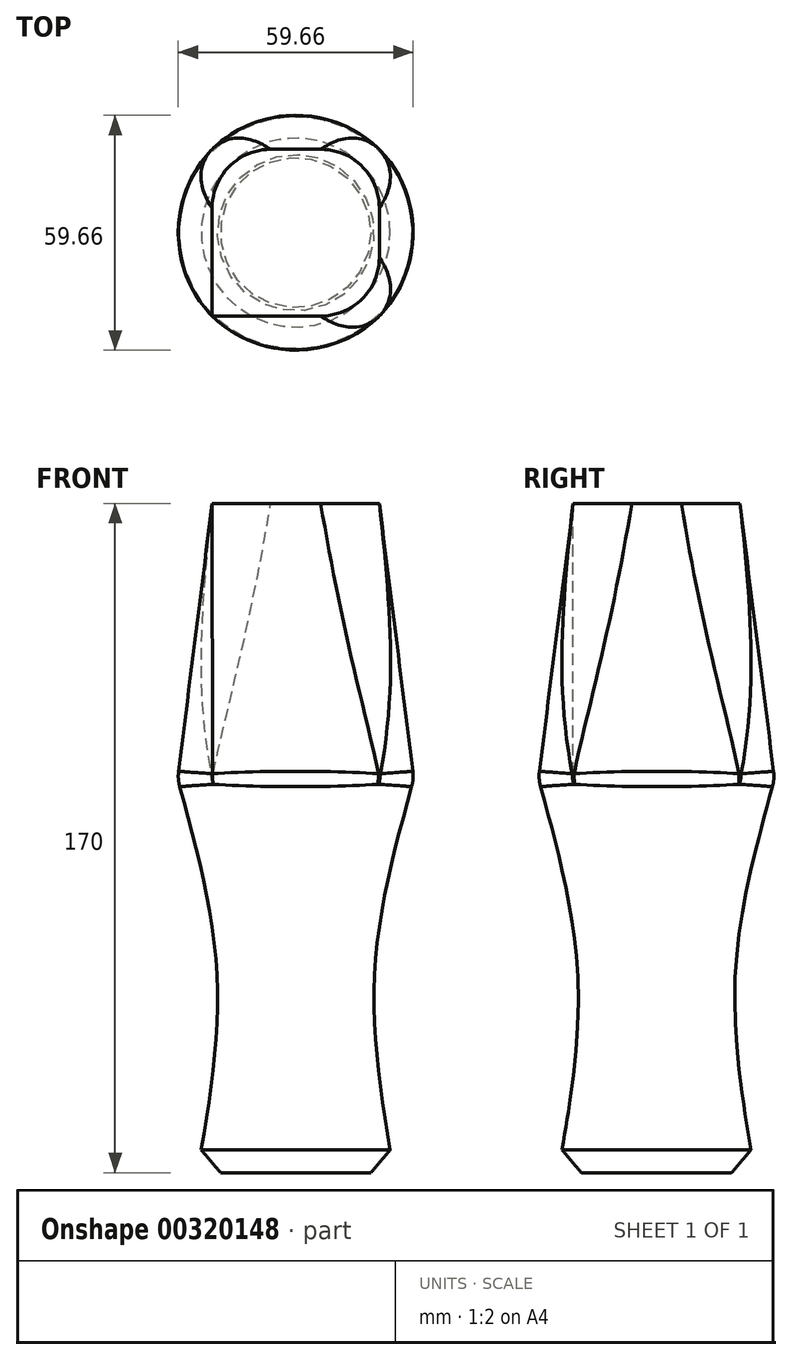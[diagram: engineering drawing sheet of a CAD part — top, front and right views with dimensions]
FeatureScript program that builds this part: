
annotation { "Feature Type Name" : "Feature", "Feature Type Description" : "" }
export const myFeature = defineFeature(function(context is Context, id is Id, definition is map)
    precondition{}
    {
        {
            var Q0;
            Q0=qCreatedBy(makeId("Top.planeOp"),FACE);
            cPlane(context, id + "F0", {"entities" : qUnion([Q0]), "cplaneType" : CPlaneType.OFFSET, "offset" : 50 * mm, "oppositeDirection" : true, "width" : 150 * mm, "height" : 150 * mm});
        }
        {
            var Q0;
            Q0=qCreatedBy(id+"F0.planeOp",FACE);
            cPlane(context, id + "F1", {"entities" : qUnion([Q0]), "cplaneType" : CPlaneType.OFFSET, "offset" : 50 * mm, "oppositeDirection" : true, "width" : 150 * mm, "height" : 150 * mm});
        }
        {
            var Q0;
            Q0=qCreatedBy(makeId("Top.planeOp"),FACE);
            var sketch = newSketch(context, id + "F2", { "sketchPlane" : qUnion([Q0])});
            skCircle(sketch, "E0", {"center": v(0, 0) * mm, "radius": 30 * mm});
            skSolve(sketch);
        }
        {
            var Q0;
            Q0=qCreatedBy(id+"F0.planeOp",FACE);
            var sketch = newSketch(context, id + "F3", { "sketchPlane" : qUnion([Q0])});
            skCircle(sketch, "E1", {"center": v(0, 0) * mm, "radius": 20 * mm});
            skSolve(sketch);
        }
        {
            var Q0;
            Q0=qCreatedBy(id+"F1.planeOp",FACE);
            var sketch = newSketch(context, id + "F4", { "sketchPlane" : qUnion([Q0])});
            skCircle(sketch, "E2", {"center": v(0, 0) * mm, "radius": 25 * mm});
            skSolve(sketch);
        }
        {
            var Q0;
            Q0 = qSketchRegion(id + "F2", true);
            var Q1;
            Q1 = qSketchRegion(id + "F3", true);
            var Q2;
            Q2 = qSketchRegion(id + "F4", true);
            loft(context, id + "F5", {"sheetProfilesArray" : [{ "sheetProfileEntities" : qUnion([Q0]) }, { "sheetProfileEntities" : qUnion([Q1]) }, { "sheetProfileEntities" : qUnion([Q2]) }]});
        }
        {
            var Q0;
            Q0=qCreatedBy(makeId("Top.planeOp"),FACE);
            cPlane(context, id + "F6", {"entities" : qUnion([Q0]), "cplaneType" : CPlaneType.OFFSET, "offset" : 70 * mm, "width" : 150 * mm, "height" : 150 * mm});
        }
        {
            var Q0;
            Q0=qCreatedBy(id+"F6.planeOp",FACE);
            var sketch = newSketch(context, id + "F7", { "sketchPlane" : qUnion([Q0])});
            skLineSegment(sketch, "E3.bottom", {"start": v(-21.25, 21.18) * mm, "end": v(21.25, 21.18) * mm});
            skLineSegment(sketch, "E3.top", {"start": v(-21.25, -21.18) * mm, "end": v(21.25, -21.18) * mm});
            skLineSegment(sketch, "E3.left", {"start": v(-21.25, -21.18) * mm, "end": v(-21.25, 21.18) * mm});
            skLineSegment(sketch, "E3.right", {"start": v(21.25, -21.18) * mm, "end": v(21.25, 21.18) * mm});
            skSolve(sketch);
        }
        {
            var Q1;
            Q1=makeQuery(id+"F5.opLoft","CAP_FACE",FACE,{"disambiguationData":[OSD([makeQuery(id+"F2.imprint","IMPRINT",FACE,{"disambiguationData":[TD([[makeQuery(id+"F2.imprint","IMPRINT",EDGE,{"derivedFrom":sQuery(id+"F2.wireOp",EDGE,"E0")}),1.0]])]})])],"isStart":true});
            var Q2;
            Q2=makeQuery(id+"F7.imprint","IMPRINT",FACE,{"disambiguationData":[TD([[makeQuery(id+"F7.imprint","IMPRINT",EDGE,{"derivedFrom":sQuery(id+"F7.wireOp",EDGE,"E3.bottom")}),-1.0]])]});
            loft(context, id + "F8", {"operationType" : NewBodyOperationType.ADD, "sheetProfilesArray" : [{ "sheetProfileEntities" : qUnion([Q1]) }, { "sheetProfileEntities" : qUnion([Q2]) }]});
        }
        {
            var Q0;
            Q0=makeQuery(id+"F8.opLoft","SWEPT_EDGE",EDGE,{"disambiguationData":[OSD([sQuery(id+"F2.wireOp",EDGE,"E0"),sQuery(id+"F7.wireOp",EDGE,"E3.top"),sQuery(id+"F7.wireOp",EDGE,"E3.left"),sQuery(id+"F7.wireOp",EDGE,"E3.right")])]});
            var Q1;
            Q1=makeQuery(id+"F8.opLoft","SWEPT_EDGE",EDGE,{"disambiguationData":[OSD([sQuery(id+"F2.wireOp",EDGE,"E0"),sQuery(id+"F7.wireOp",EDGE,"E3.bottom"),sQuery(id+"F7.wireOp",EDGE,"E3.top"),sQuery(id+"F7.wireOp",EDGE,"E3.right")])]});
            var Q2;
            Q2=makeQuery(id+"F8.opLoft","SWEPT_EDGE",EDGE,{"disambiguationData":[OSD([sQuery(id+"F2.wireOp",EDGE,"E0"),sQuery(id+"F7.wireOp",EDGE,"E3.bottom"),sQuery(id+"F7.wireOp",EDGE,"E3.top"),sQuery(id+"F7.wireOp",EDGE,"E3.left")])]});
            var Q3;
            Q3=makeQuery(id+"F8.opLoft","SWEPT_EDGE",EDGE,{"disambiguationData":[OSD([sQuery(id+"F7.wireOp",EDGE,"E3.bottom"),sQuery(id+"F7.wireOp",EDGE,"E3.left")])]});
            fillet(context, id + "F9", {"entities" : qUnion([Q0, Q1, Q2, Q3]), "radius" : 15 * mm, "tangentPropagation" : true, "allowEdgeOverflow" : false});
        }
        {
            var Q0;
            {var subQ0=sQuery(id+"F2.wireOp",EDGE,"E0");Q0=makeQuery(id+"F8.boolean.opBoolean","MERGE",EDGE,{"derivedFrom":[makeQuery(id+"F5.opLoft","MID_CAP_EDGE",EDGE,{"disambiguationData":[OSD([subQ0])],"capPos":0.0}),makeQuery(id+"F8.opLoft","MID_CAP_EDGE",EDGE,{"disambiguationData":[OSD([subQ0,sQuery(id+"F7.wireOp",EDGE,"E3.bottom"),sQuery(id+"F7.wireOp",EDGE,"E3.left")])],"capPos":0.0})]});}
            fillet(context, id + "F10", {"entities" : qUnion([Q0]), "radius" : 10 * mm, "tangentPropagation" : true, "allowEdgeOverflow" : false});
        }
        {
            var Q0;
            Q0=makeQuery(id+"F5.opLoft","CAP_FACE",FACE,{"disambiguationData":[OSD([makeQuery(id+"F4.imprint","IMPRINT",FACE,{"disambiguationData":[TD([[makeQuery(id+"F4.imprint","IMPRINT",EDGE,{"derivedFrom":sQuery(id+"F4.wireOp",EDGE,"E2")}),1.0]])]})])],"isStart":true});
            chamfer(context, id + "F11", {"entities" : qUnion([Q0]), "width" : 5 * mm, "tangentPropagation" : true});
        }
    });
